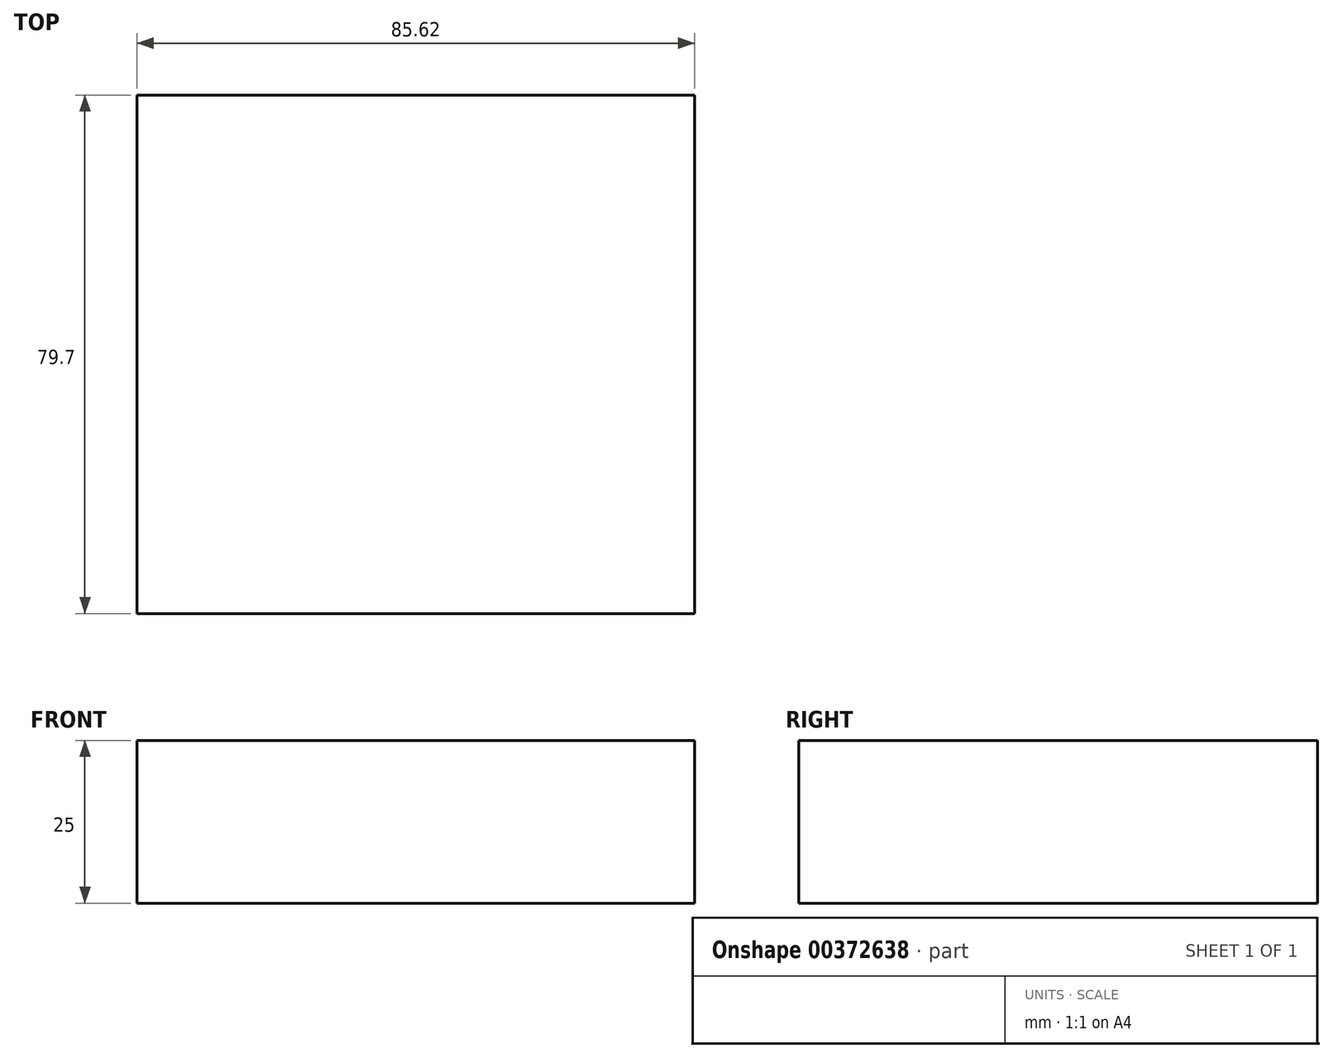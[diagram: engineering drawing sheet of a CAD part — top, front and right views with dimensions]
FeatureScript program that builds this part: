
annotation { "Feature Type Name" : "Feature", "Feature Type Description" : "" }
export const myFeature = defineFeature(function(context is Context, id is Id, definition is map)
    precondition{}
    {
        {
            var Q0;
            Q0=qCreatedBy(makeId("Top.planeOp"),FACE);
            var sketch = newSketch(context, id + "F0", { "sketchPlane" : qUnion([Q0])});
            skLineSegment(sketch, "E0.bottom", {"start": v(42.81, -39.85) * mm, "end": v(-42.81, -39.85) * mm});
            skLineSegment(sketch, "E0.top", {"start": v(42.81, 39.85) * mm, "end": v(-42.81, 39.85) * mm});
            skLineSegment(sketch, "E0.left", {"start": v(42.81, -39.85) * mm, "end": v(42.81, 39.85) * mm});
            skLineSegment(sketch, "E0.right", {"start": v(-42.81, -39.85) * mm, "end": v(-42.81, 39.85) * mm});
            skPoint(sketch, "E0.middle", {"position": v(0, 0) * mm});
            skSolve(sketch);
        }
        {
            var Q0;
            Q0=makeQuery(id+"F0.imprint","IMPRINT",FACE,{"disambiguationData":[TD([[makeQuery(id+"F0.imprint","IMPRINT",EDGE,{"derivedFrom":sQuery(id+"F0.wireOp",EDGE,"E0.bottom")}),-1.0]])]});
            extrude(context, id + "F1", {"entities" : qUnion([Q0]), "depth" : 25 * mm});
        }
    });
